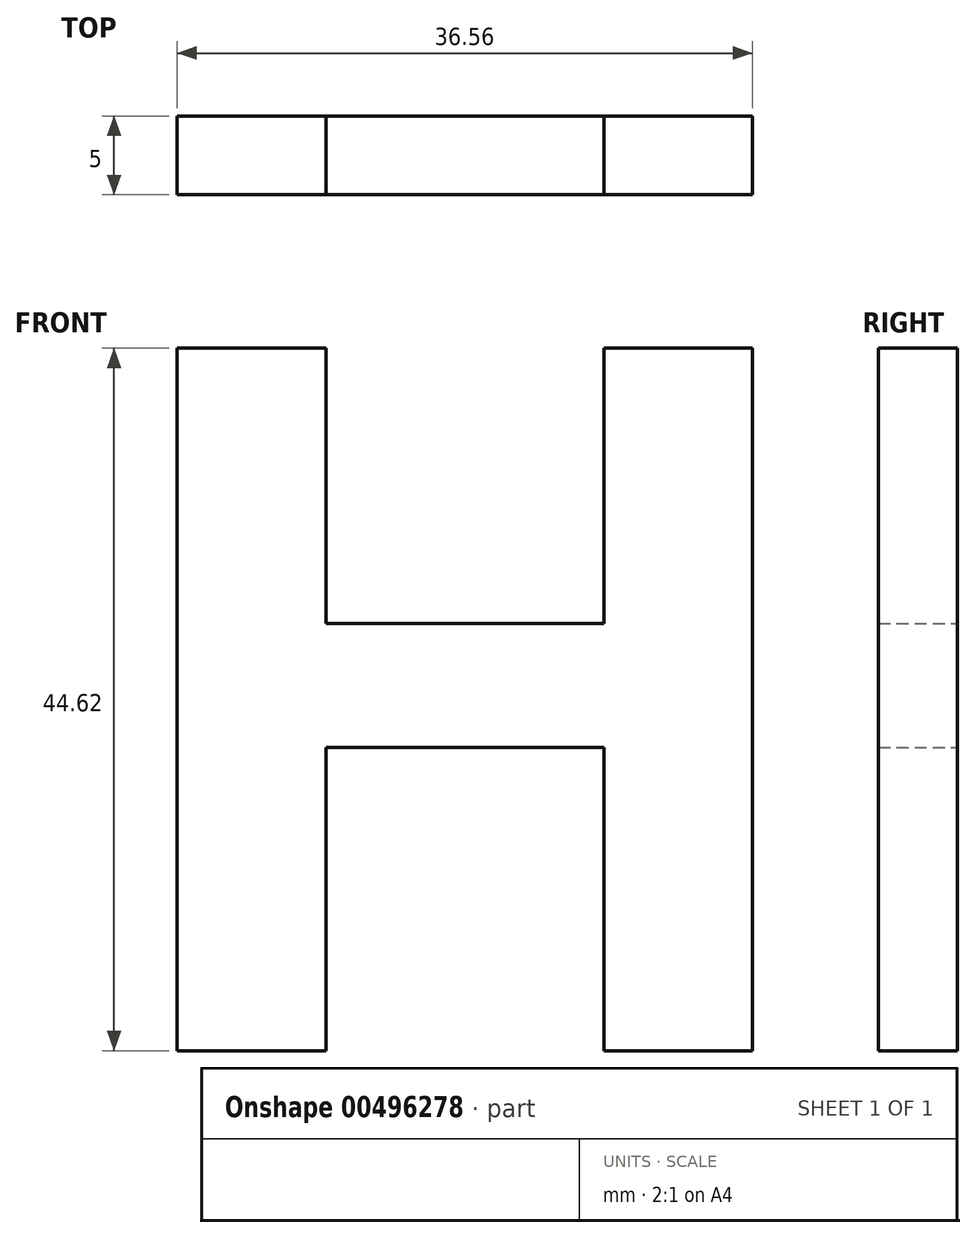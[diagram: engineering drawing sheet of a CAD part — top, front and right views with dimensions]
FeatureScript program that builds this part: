
annotation { "Feature Type Name" : "Feature", "Feature Type Description" : "" }
export const myFeature = defineFeature(function(context is Context, id is Id, definition is map)
    precondition{}
    {
        {
            var Q0;
            Q0=qCreatedBy(makeId("Front.planeOp"),FACE);
            var sketch = newSketch(context, id + "F0", { "sketchPlane" : qUnion([Q0])});
            skText(sketch, "E0", { "text": "H", "fontName": "OpenSans-Bold.ttf"});
            const initialGuessF0  = {"E0": [-0.06951, 0.02426, 1, 0, 0.045]};
            skSetInitialGuess(sketch, initialGuessF0);
            skSolve(sketch);
        }
        {
            var Q0;
            Q0=makeQuery(id+"F0.imprint","IMPRINT",FACE,{"disambiguationData":[TD([[makeQuery(id+"F0.imprint","IMPRINT",EDGE,{"derivedFrom":sQuery(id+"F0.wireOp",EDGE,"E0.sketch_text.stroke-0")}),-1.0]])]});
            extrude(context, id + "F1", {"entities" : qUnion([Q0]), "depth" : 5 * mm});
        }
    });
